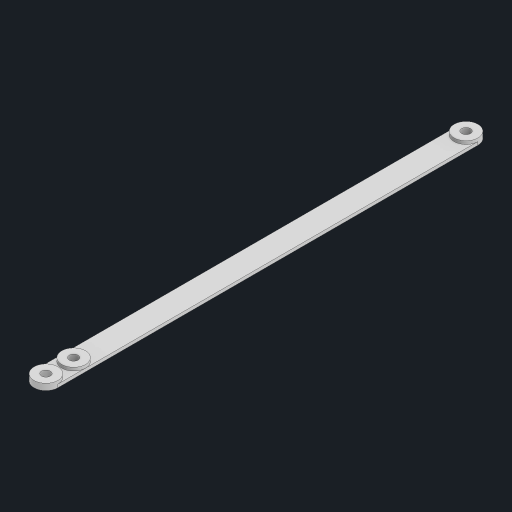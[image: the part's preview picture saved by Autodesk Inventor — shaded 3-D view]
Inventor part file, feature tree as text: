
AUTODESK INVENTOR PART (.ipt)
format: ipt  version: 2023 (Build 270158000, 158)  size: 117,760 bytes
history: native  units: mm
features: extrude x2, sketch x1
ambient origin geometry x8: Origin, YZ Plane, XZ Plane, XY Plane, X Axis, Y Axis, Z Axis, Center Point
bodies: Solid1 (feature_tree)
feature tree (3):
  sketch  "Sketch1"  dims[d0=15.0mm d1=5.5mm d7=15.0mm d10=4.0mm d11=0.0mm d12=15.0mm d13=5.5mm d14=2.0mm d15=0.0mm d17=262.97mm d18=15.0mm d19=2.5mm d22=15.0mm d23=5.5mm d24=0.5mm d25=0.872665mm d26=0.5mm d27=0.872665mm]
  extrude  "Extrusion2"  Depth=15.0mm
  extrude  "Extrusion3"  Depth=15.0mm
